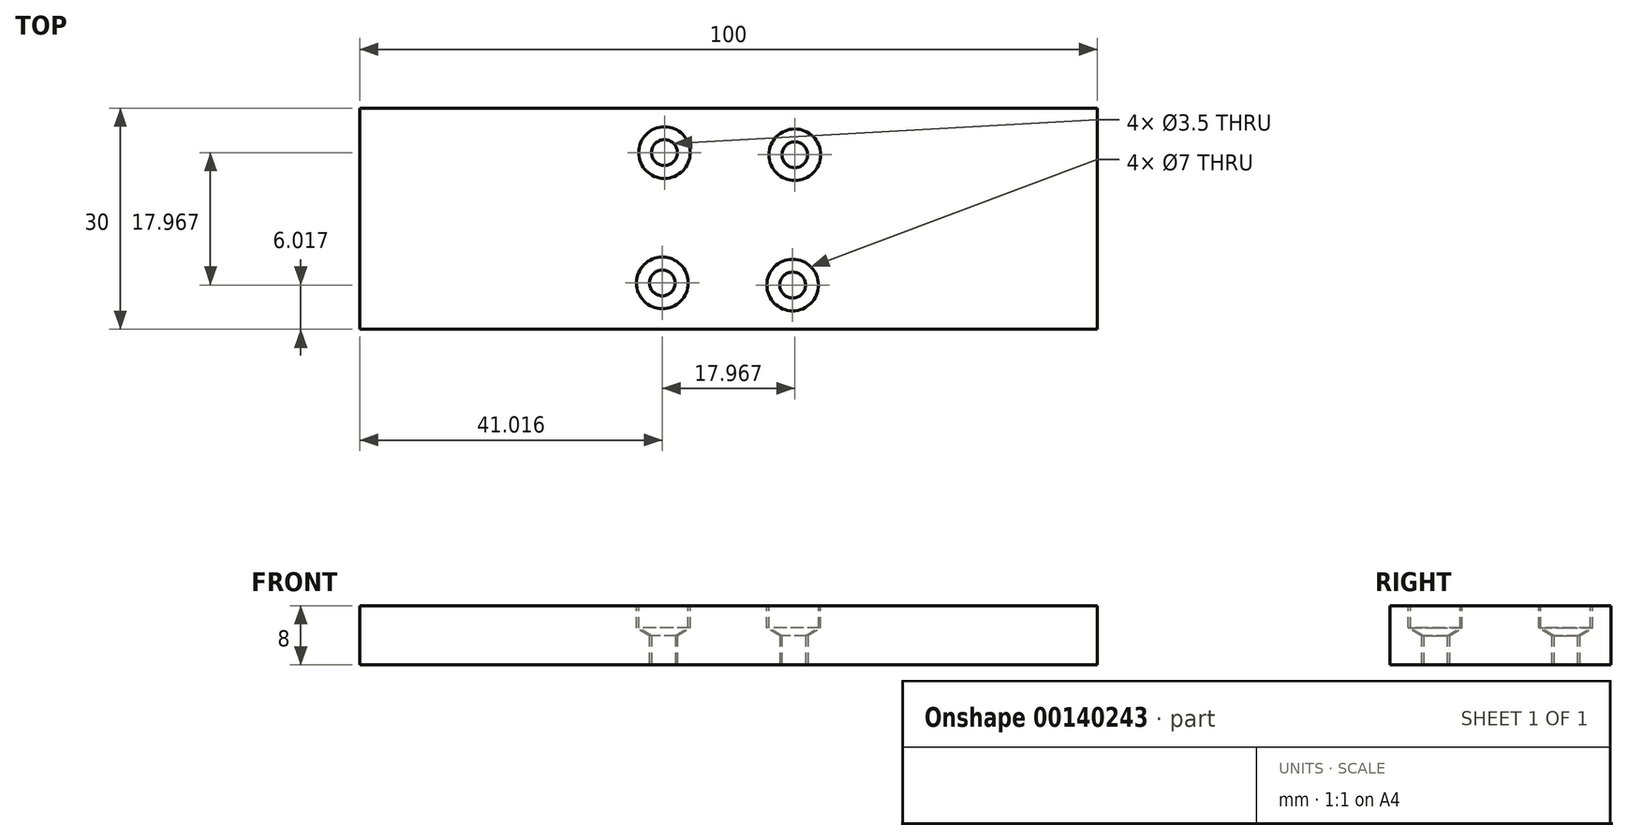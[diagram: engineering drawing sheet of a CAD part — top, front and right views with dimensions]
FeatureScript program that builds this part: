
annotation { "Feature Type Name" : "Feature", "Feature Type Description" : "" }
export const myFeature = defineFeature(function(context is Context, id is Id, definition is map)
    precondition{}
    {
        {
            var Q0;
            Q0=qCreatedBy(makeId("Top.planeOp"),FACE);
            var sketch = newSketch(context, id + "F0", { "sketchPlane" : qUnion([Q0])});
            skLineSegment(sketch, "E0.bottom", {"start": v(-59.18, -13.34) * mm, "end": v(40.82, -13.34) * mm});
            skLineSegment(sketch, "E0.top", {"start": v(-59.18, 16.66) * mm, "end": v(40.82, 16.66) * mm});
            skLineSegment(sketch, "E0.left", {"start": v(-59.18, -13.34) * mm, "end": v(-59.18, 16.66) * mm});
            skLineSegment(sketch, "E0.right", {"start": v(40.82, -13.34) * mm, "end": v(40.82, 16.66) * mm});
            skCircle(sketch, "E1", {"center": v(-17.87, 10.64) * mm, "radius": 1.75 * mm});
            skCircle(sketch, "E2", {"center": v(-0.2, 10.35) * mm, "radius": 1.75 * mm});
            skCircle(sketch, "E3", {"center": v(-0.49, -7.32) * mm, "radius": 1.75 * mm});
            skCircle(sketch, "E4", {"center": v(-18.16, -7.03) * mm, "radius": 1.75 * mm});
            skLineSegment(sketch, "E5", {"start": v(-17.87, 10.64) * mm, "end": v(-0.49, -7.32) * mm});
            skLineSegment(sketch, "E6", {"start": v(-0.2, 10.35) * mm, "end": v(-18.16, -7.03) * mm});
            skPoint(sketch, "E7", {"position": v(-9.18, 1.66) * mm});
            skSolve(sketch);
        }
        {
            var Q0;
            Q0=makeQuery(id+"F0.imprint","IMPRINT",FACE,{"disambiguationData":[TD([[makeQuery(id+"F0.imprint","IMPRINT",EDGE,{"derivedFrom":sQuery(id+"F0.wireOp",EDGE,"E0.bottom")}),1.0]])]});
            extrude(context, id + "F1", {"entities" : qUnion([Q0]), "depth" : 8 * mm});
        }
        {
            var Q0;
            Q0=makeQuery(id+"F1.opExtrude","CAP_FACE",FACE,{"disambiguationData":[OSD([sQuery(id+"F0.wireOp",EDGE,"E0.bottom"),sQuery(id+"F0.wireOp",EDGE,"E0.top"),sQuery(id+"F0.wireOp",EDGE,"E0.left"),sQuery(id+"F0.wireOp",EDGE,"E0.right"),sQuery(id+"F0.wireOp",EDGE,"E1"),sQuery(id+"F0.wireOp",EDGE,"E2"),sQuery(id+"F0.wireOp",EDGE,"E3"),sQuery(id+"F0.wireOp",EDGE,"E4")])],"isStart":false});
            var sketch = newSketch(context, id + "F2", { "sketchPlane" : qUnion([Q0])});
            skPoint(sketch, "E8", {"position": v(-18.16, -7.03) * mm});
            skPoint(sketch, "E9", {"position": v(-0.49, -7.32) * mm});
            skPoint(sketch, "E10", {"position": v(-0.2, 10.35) * mm});
            skPoint(sketch, "E11", {"position": v(-17.87, 10.64) * mm});
            skSolve(sketch);
        }
        {
            var Q0;
            Q0=sQuery(id+"F2.wireOp",VERTEX,"E9");
            var Q1;
            Q1=sQuery(id+"F2.wireOp",VERTEX,"E8");
            var Q2;
            Q2=sQuery(id+"F2.wireOp",VERTEX,"E11");
            var Q3;
            Q3=sQuery(id+"F2.wireOp",VERTEX,"E10");
            var Q4;
            Q4=makeQuery(id+"F1.opExtrude","SWEPT_BODY",BODY,{"disambiguationData":[OSD([sQuery(id+"F0.wireOp",EDGE,"E0.bottom"),sQuery(id+"F0.wireOp",EDGE,"E0.top"),sQuery(id+"F0.wireOp",EDGE,"E0.left"),sQuery(id+"F0.wireOp",EDGE,"E0.right"),sQuery(id+"F0.wireOp",EDGE,"E1"),sQuery(id+"F0.wireOp",EDGE,"E2"),sQuery(id+"F0.wireOp",EDGE,"E3"),sQuery(id+"F0.wireOp",EDGE,"E4")])]});
            hole(context, id + "F3", {"style" : HoleStyle.SIMPLE, "endStyle" : HoleEndStyle.BLIND, "holeDiameter" : 7 * mm, "holeDepth" : 3 * mm, "locations" : qUnion([Q0, Q1, Q2, Q3]), "scope" : qUnion([Q4])});
        }
    });
